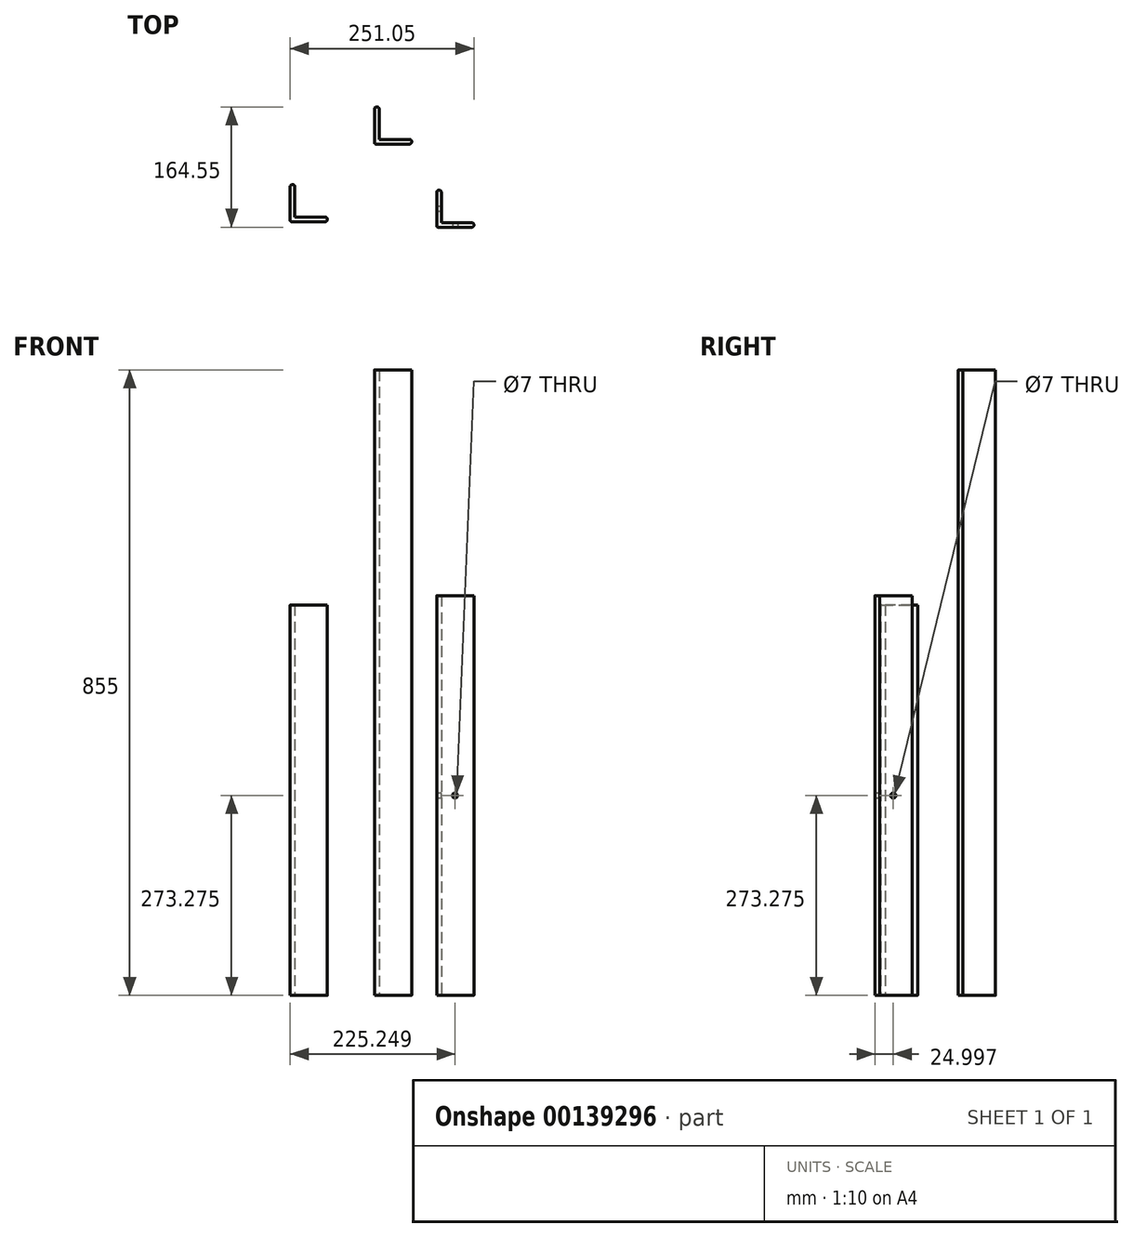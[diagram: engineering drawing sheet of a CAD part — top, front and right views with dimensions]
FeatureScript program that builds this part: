
annotation { "Feature Type Name" : "Feature", "Feature Type Description" : "" }
export const myFeature = defineFeature(function(context is Context, id is Id, definition is map)
    precondition{}
    {
        {
            var Q0;
            Q0=qCreatedBy(makeId("Top.planeOp"),FACE);
            var sketch = newSketch(context, id + "F0", { "sketchPlane" : qUnion([Q0])});
            skLineSegment(sketch, "E0", {"start": v(0, 0) * mm, "end": v(0, 50.8) * mm});
            skLineSegment(sketch, "E1", {"start": v(0, 0) * mm, "end": v(50.8, 0) * mm});
            skLineSegment(sketch, "E2", {"start": v(50.8, 0) * mm, "end": v(50.8, 6.35) * mm});
            skLineSegment(sketch, "E3", {"start": v(50.8, 6.35) * mm, "end": v(6.35, 6.35) * mm});
            skLineSegment(sketch, "E4", {"start": v(0, 50.8) * mm, "end": v(6.35, 50.8) * mm});
            skLineSegment(sketch, "E5", {"start": v(6.35, 50.8) * mm, "end": v(6.35, 6.35) * mm});
            skLineSegment(sketch, "E6", {"start": v(85.05, -113.75) * mm, "end": v(85.05, -62.95) * mm});
            skLineSegment(sketch, "E7", {"start": v(85.05, -113.75) * mm, "end": v(135.85, -113.75) * mm});
            skLineSegment(sketch, "E8", {"start": v(135.85, -113.75) * mm, "end": v(135.85, -107.4) * mm});
            skLineSegment(sketch, "E9", {"start": v(135.85, -107.4) * mm, "end": v(91.4, -107.4) * mm});
            skLineSegment(sketch, "E10", {"start": v(85.05, -62.95) * mm, "end": v(91.4, -62.95) * mm});
            skLineSegment(sketch, "E11", {"start": v(91.4, -62.95) * mm, "end": v(91.4, -107.4) * mm});
            skLineSegment(sketch, "E12", {"start": v(-115.2, -106.15) * mm, "end": v(-115.2, -55.35) * mm});
            skLineSegment(sketch, "E13", {"start": v(-115.2, -106.15) * mm, "end": v(-64.4, -106.15) * mm});
            skLineSegment(sketch, "E14", {"start": v(-64.4, -106.15) * mm, "end": v(-64.4, -99.8) * mm});
            skLineSegment(sketch, "E15", {"start": v(-64.4, -99.8) * mm, "end": v(-108.85, -99.8) * mm});
            skLineSegment(sketch, "E16", {"start": v(-115.2, -55.35) * mm, "end": v(-108.85, -55.35) * mm});
            skLineSegment(sketch, "E17", {"start": v(-108.85, -55.35) * mm, "end": v(-108.85, -99.8) * mm});
            skSolve(sketch);
        }
        {
            var Q0;
            Q0=makeQuery(id+"F0.imprint","IMPRINT",FACE,{"disambiguationData":[TD([[makeQuery(id+"F0.imprint","IMPRINT",EDGE,{"derivedFrom":sQuery(id+"F0.wireOp",EDGE,"E0")}),-1.0]])]});
            extrude(context, id + "F1", {"entities" : qUnion([Q0]), "depth" : 855 * mm});
        }
        {
            var Q0;
            Q0=makeQuery(id+"F0.imprint","IMPRINT",FACE,{"disambiguationData":[TD([[makeQuery(id+"F0.imprint","IMPRINT",EDGE,{"derivedFrom":sQuery(id+"F0.wireOp",EDGE,"E6")}),-1.0]])]});
            extrude(context, id + "F2", {"entities" : qUnion([Q0]), "depth" : 546.55 * mm});
        }
        {
            var Q0;
            Q0=makeQuery(id+"F0.imprint","IMPRINT",FACE,{"disambiguationData":[TD([[makeQuery(id+"F0.imprint","IMPRINT",EDGE,{"derivedFrom":sQuery(id+"F0.wireOp",EDGE,"E12")}),-1.0]])]});
            extrude(context, id + "F3", {"entities" : qUnion([Q0]), "depth" : 533.85 * mm});
        }
        {
            var Q0;
            Q0=makeQuery(id+"F2.opExtrude","SWEPT_FACE",FACE,{"disambiguationData":[OSD([sQuery(id+"F0.wireOp",EDGE,"E6")])]});
            var sketch = newSketch(context, id + "F4", { "sketchPlane" : qUnion([Q0])});
            skLineSegment(sketch, "E18", {"start": v(113.75, 546.55) * mm, "end": v(113.75, 273.27) * mm});
            skLineSegment(sketch, "E19", {"start": v(113.75, 273.27) * mm, "end": v(88.75, 273.27) * mm});
            skCircle(sketch, "E20", {"center": v(88.75, 273.27) * mm, "radius": 3.5 * mm});
            skSolve(sketch);
        }
        {
            var Q0;
            Q0=makeQuery(id+"F4.imprint","IMPRINT",FACE,{"disambiguationData":[TD([[makeQuery(id+"F4.imprint","IMPRINT",EDGE,{"derivedFrom":sQuery(id+"F4.wireOp",EDGE,"E20")}),1.0]])]});
            var Q1;
            Q1=makeQuery(id+"F2.opExtrude","SWEPT_FACE",FACE,{"disambiguationData":[OSD([sQuery(id+"F0.wireOp",EDGE,"E11")])]});
            extrude(context, id + "F5", {"entities" : qUnion([Q0]), "operationType" : NewBodyOperationType.REMOVE, "endBound" : BoundingType.UP_TO_SURFACE, "oppositeDirection" : true, "endBoundEntityFace" : qUnion([Q1]), "depth" : 25 * mm});
        }
        {
            var Q0;
            Q0=makeQuery(id+"F2.opExtrude","SWEPT_FACE",FACE,{"disambiguationData":[OSD([sQuery(id+"F0.wireOp",EDGE,"E7")])]});
            var sketch = newSketch(context, id + "F6", { "sketchPlane" : qUnion([Q0])});
            skLineSegment(sketch, "E21", {"start": v(85.05, 273.27) * mm, "end": v(110.05, 273.27) * mm});
            skCircle(sketch, "E22", {"center": v(110.05, 273.27) * mm, "radius": 3.5 * mm});
            skSolve(sketch);
        }
        {
            var Q0;
            Q0=makeQuery(id+"F6.imprint","IMPRINT",FACE,{"disambiguationData":[TD([[makeQuery(id+"F6.imprint","IMPRINT",EDGE,{"derivedFrom":sQuery(id+"F6.wireOp",EDGE,"E22")}),1.0]])]});
            var Q1;
            Q1=makeQuery(id+"F2.opExtrude","SWEPT_FACE",FACE,{"disambiguationData":[OSD([sQuery(id+"F0.wireOp",EDGE,"E9")])]});
            extrude(context, id + "F7", {"entities" : qUnion([Q0]), "operationType" : NewBodyOperationType.REMOVE, "endBound" : BoundingType.UP_TO_SURFACE, "oppositeDirection" : true, "endBoundEntityFace" : qUnion([Q1]), "depth" : 25 * mm});
        }
        {
            var Q0;
            Q0=makeQuery(id+"F3.opExtrude","SWEPT_EDGE",EDGE,{"disambiguationData":[OSD([sQuery(id+"F0.wireOp",EDGE,"E13"),sQuery(id+"F0.wireOp",EDGE,"E14")])]});
            var Q1;
            Q1=makeQuery(id+"F3.opExtrude","SWEPT_EDGE",EDGE,{"disambiguationData":[OSD([sQuery(id+"F0.wireOp",EDGE,"E14"),sQuery(id+"F0.wireOp",EDGE,"E15")])]});
            var Q2;
            Q2=makeQuery(id+"F3.opExtrude","SWEPT_EDGE",EDGE,{"disambiguationData":[OSD([sQuery(id+"F0.wireOp",EDGE,"E16"),sQuery(id+"F0.wireOp",EDGE,"E17")])]});
            var Q3;
            Q3=makeQuery(id+"F3.opExtrude","SWEPT_EDGE",EDGE,{"disambiguationData":[OSD([sQuery(id+"F0.wireOp",EDGE,"E12"),sQuery(id+"F0.wireOp",EDGE,"E16")])]});
            var Q4;
            Q4=makeQuery(id+"F2.opExtrude","SWEPT_EDGE",EDGE,{"disambiguationData":[OSD([sQuery(id+"F0.wireOp",EDGE,"E7"),sQuery(id+"F0.wireOp",EDGE,"E8")])]});
            var Q5;
            Q5=makeQuery(id+"F2.opExtrude","SWEPT_EDGE",EDGE,{"disambiguationData":[OSD([sQuery(id+"F0.wireOp",EDGE,"E6"),sQuery(id+"F0.wireOp",EDGE,"E10")])]});
            var Q6;
            Q6=makeQuery(id+"F2.opExtrude","SWEPT_EDGE",EDGE,{"disambiguationData":[OSD([sQuery(id+"F0.wireOp",EDGE,"E10"),sQuery(id+"F0.wireOp",EDGE,"E11")])]});
            var Q7;
            Q7=makeQuery(id+"F2.opExtrude","SWEPT_EDGE",EDGE,{"disambiguationData":[OSD([sQuery(id+"F0.wireOp",EDGE,"E8"),sQuery(id+"F0.wireOp",EDGE,"E9")])]});
            var Q8;
            Q8=makeQuery(id+"F1.opExtrude","SWEPT_EDGE",EDGE,{"disambiguationData":[OSD([sQuery(id+"F0.wireOp",EDGE,"E4"),sQuery(id+"F0.wireOp",EDGE,"E5")])]});
            var Q9;
            Q9=makeQuery(id+"F1.opExtrude","SWEPT_EDGE",EDGE,{"disambiguationData":[OSD([sQuery(id+"F0.wireOp",EDGE,"E0"),sQuery(id+"F0.wireOp",EDGE,"E4")])]});
            var Q10;
            Q10=makeQuery(id+"F1.opExtrude","SWEPT_EDGE",EDGE,{"disambiguationData":[OSD([sQuery(id+"F0.wireOp",EDGE,"E2"),sQuery(id+"F0.wireOp",EDGE,"E3")])]});
            var Q11;
            Q11=makeQuery(id+"F1.opExtrude","SWEPT_EDGE",EDGE,{"disambiguationData":[OSD([sQuery(id+"F0.wireOp",EDGE,"E1"),sQuery(id+"F0.wireOp",EDGE,"E2")])]});
            fillet(context, id + "F8", {"entities" : qUnion([Q0, Q1, Q2, Q3, Q4, Q5, Q6, Q7, Q8, Q9, Q10, Q11]), "radius" : 3 * mm, "tangentPropagation" : true, "allowEdgeOverflow" : false});
        }
        {
            var Q0;
            Q0=makeQuery(id+"F3.opExtrude","SWEPT_EDGE",EDGE,{"disambiguationData":[OSD([sQuery(id+"F0.wireOp",EDGE,"E12"),sQuery(id+"F0.wireOp",EDGE,"E13")])]});
            var Q1;
            Q1=makeQuery(id+"F2.opExtrude","SWEPT_EDGE",EDGE,{"disambiguationData":[OSD([sQuery(id+"F0.wireOp",EDGE,"E6"),sQuery(id+"F0.wireOp",EDGE,"E7")])]});
            var Q2;
            Q2=makeQuery(id+"F1.opExtrude","SWEPT_EDGE",EDGE,{"disambiguationData":[OSD([sQuery(id+"F0.wireOp",EDGE,"E0"),sQuery(id+"F0.wireOp",EDGE,"E1")])]});
            fillet(context, id + "F9", {"entities" : qUnion([Q0, Q1, Q2]), "radius" : 2 * mm, "tangentPropagation" : true, "allowEdgeOverflow" : false});
        }
    });
